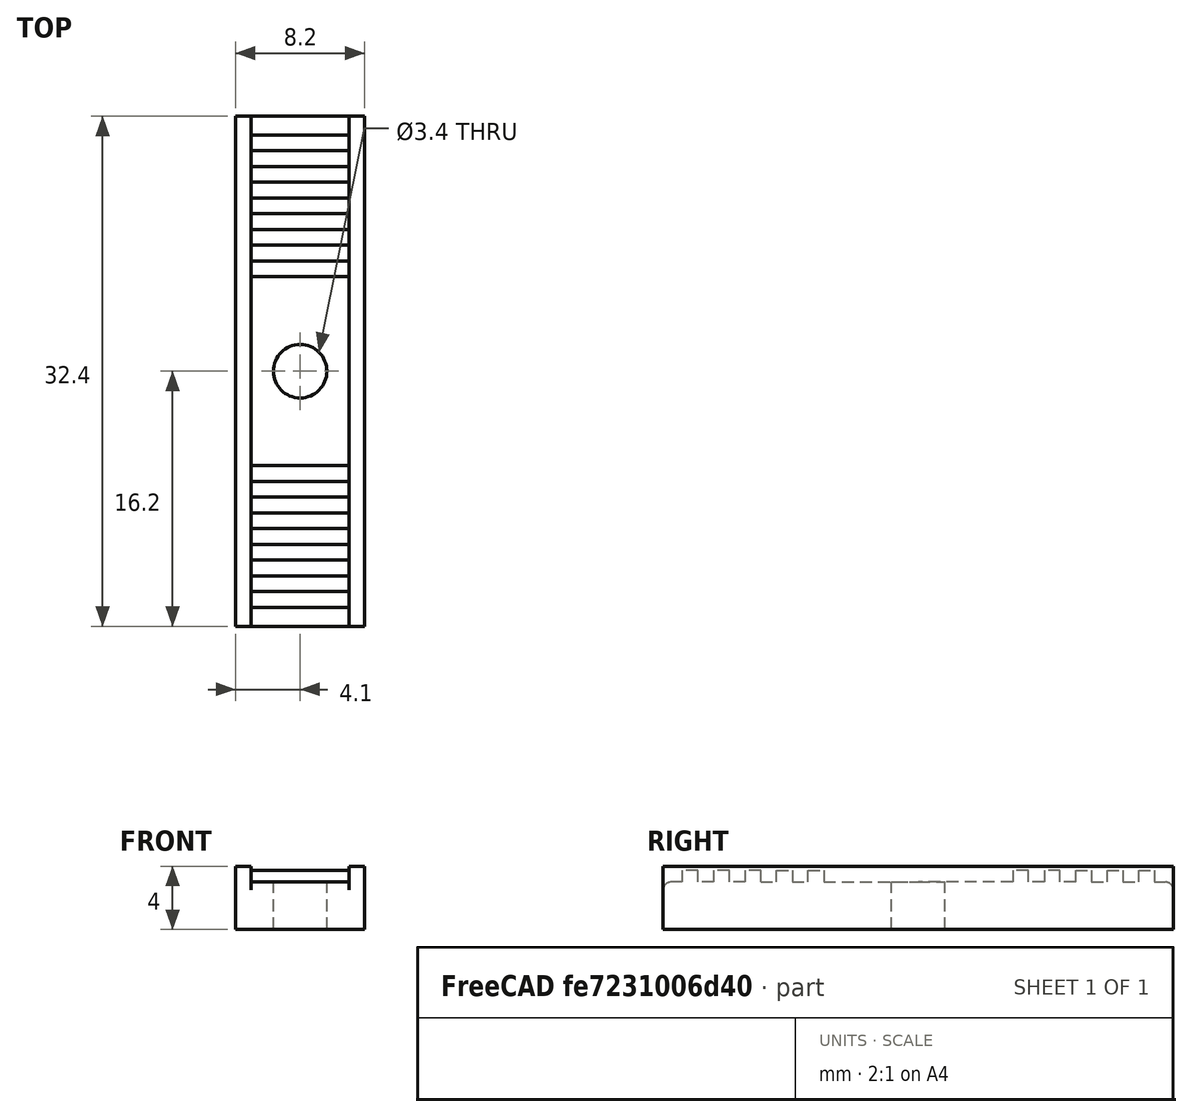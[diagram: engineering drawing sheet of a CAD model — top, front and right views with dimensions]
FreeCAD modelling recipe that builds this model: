
FCSTD DOCUMENT  (FreeCAD 2022.709R28846 (Git))
Label: X_Joiner
License: All rights reserved
LicenseURL: http://en.wikipedia.org/wiki/All_rights_reserved
objects: Sketcher::SketchObject×3, PartDesign::Pad×3, PartDesign::Hole×3, Part::Feature×2, PartDesign::Plane×2, App::DocumentObjectGroup×2, PartDesign::SubShapeBinder×2, PartDesign::Body×2, PartDesign::Fillet×2, Sketcher::SketchExport×2, Spreadsheet::Sheet×1, PartDesign::Mirrored×1, PartDesign::Boolean×1
note: 42 computed .brp shape members not serialized (recipe doc carries the construction recipe); baked Part::Feature solids carry a one-line shape summary decoded from their .brp

FEATURE [Spreadsheet::Sheet] Spreadsheet  label="Variables"
  PythonMode = false
  ShowCells = 0
  TreeRank = 15
  cells = A2=CarriageEdgeToBelt; B2(CarriageEdgeToBelt)==2mm
FEATURE [Part::Feature] XJoint_right_bottom001
  TreeRank = 17
  shape: bbox 38.03 x 54.61 x 16.83 mm, 16460 faces, 0 solids (baked)
FEATURE [PartDesign::Plane] DatumPlane
  AttachmentSupport = -> [XJoint_right_bottom001]
  Length = 49.5
  MapMode = 5
  MinimumLength = 10
  MinimumWidth = 10
  Placement = pos=(0,0,13) rot=(1,0,0;3.14159rad)
  ResizeMode = 0
  Support = -> [XJoint_right_bottom001]
  TreeRank = 13
  Width = 54.5803
FEATURE [Part::Feature] XJoint_right_bottom001_solid  label="XJoint_right_bottom001 (Solid)"
  TreeRank = 26
  shape: bbox 38.03 x 54.61 x 16.83 mm, 16460 faces (baked)
FEATURE [App::DocumentObjectGroup] Group001  label="Base Mesh"
  ClaimAllChildren = true
  ExportMode = 1
  Group = -> [XJoint_right_bottom001]
  TreeRank = 23
  _GroupVersion = 1
FEATURE [PartDesign::SubShapeBinder] Binder  label="Binder(HeatsetLocation)"
  BindCopyOnChange = 0
  BindMode = 0
  ClaimChildren = false
  Context = -> Group [Body.Binder.]
  FillStyle = 0
  Fuse = false
  MakeFace = true
  OffsetFill = false
  OffsetIntersection = false
  OffsetJoinType = 0
  OffsetOpenResult = false
  PartialLoad = false
  Placement = pos=(0,0,6.6) rot=(0,0,1;0rad)
  Relative = true
  Support = -> [Export]
  TreeRank = 27
  _Version = 8
  expr: Placement.Base.z = <<Pad>>.Length
FEATURE [PartDesign::Plane] DatumPlane001
  AttachmentSupport = -> [YZ_Plane001]
  Length = 16.2
  MapMode = 5
  MinimumLength = 10
  MinimumWidth = 10
  Placement = pos=(0,0,0) rot=(0.57735,0.57735,0.57735;2.0944rad)
  ResizeMode = 0
  Support = -> [YZ_Plane001]
  TreeRank = 40
  Width = 10
FEATURE [Sketcher::SketchObject] Sketch001
  ArcFitTolerance = 1e-06
  AttachmentSupport = -> [DatumPlane001]
  FullyConstrained = true
  MapMode = 5
  Placement = pos=(0,0,0) rot=(0.57735,0.57735,0.57735;2.0944rad)
  Support = -> [DatumPlane001]
  TreeRank = 41
  expr: Constraints[50] = <<Sketch>>.Constraints.Length / 2
  expr: Constraints[61] = <<Sketch>>.Constraints[<<Belt Dist>>] / 2
  sketch-geometry (31):
    g0: LineSegment StartX=-10 StartY=3 StartZ=0 EndX=-9 EndY=3 EndZ=0
    g1: LineSegment StartX=-9 StartY=3 StartZ=0 EndX=-9 EndY=3.75 EndZ=0
    g2: LineSegment StartX=-9 StartY=3.75 StartZ=0 EndX=-8 EndY=3.75 EndZ=0
    g3: LineSegment StartX=-8 StartY=3.75 StartZ=0 EndX=-8 EndY=3 EndZ=0
    g4: LineSegment StartX=-7 StartY=3 StartZ=0 EndX=-7 EndY=3.75 EndZ=0
    g5: LineSegment StartX=-10 StartY=3 StartZ=0 EndX=-10 EndY=3.75 EndZ=0
    g6: LineSegment StartX=-10 StartY=3.75 StartZ=0 EndX=-11 EndY=3.75 EndZ=0
    g7: LineSegment StartX=-11 StartY=3.75 StartZ=0 EndX=-11 EndY=3 EndZ=0
    g8: LineSegment StartX=-11 StartY=3 StartZ=0 EndX=-12 EndY=3 EndZ=0
    g9: LineSegment StartX=-12 StartY=3 StartZ=0 EndX=-12 EndY=3.75 EndZ=0
    g10: LineSegment StartX=-12 StartY=3.75 StartZ=0 EndX=-13 EndY=3.75 EndZ=0
    g11: LineSegment StartX=-13 StartY=3.75 StartZ=0 EndX=-13 EndY=3 EndZ=0
    g12: LineSegment [constr] StartX=-12 StartY=3.75 StartZ=0 EndX=-11 EndY=3.75 EndZ=0
    g13: LineSegment [constr] StartX=-10 StartY=3.75 StartZ=0 EndX=-9 EndY=3.75 EndZ=0
    g14: LineSegment [constr] StartX=-8 StartY=3.75 StartZ=0 EndX=-7 EndY=3.75 EndZ=0
    g15: LineSegment [constr] StartX=-10 StartY=3 StartZ=0 EndX=-11 EndY=3 EndZ=0
    g16: LineSegment [constr] StartX=-12 StartY=3 StartZ=0 EndX=-13 EndY=3 EndZ=0
    g17: LineSegment StartX=-16.2 StartY=2.5 StartZ=0 EndX=-16.2 EndY=0 EndZ=0
    g18: LineSegment StartX=-16.2 StartY=0 StartZ=0 EndX=0 EndY=0 EndZ=0
    g19: LineSegment StartX=0 StartY=0 StartZ=0 EndX=0 EndY=3 EndZ=0
    g20: LineSegment StartX=-8 StartY=3 StartZ=0 EndX=-7 EndY=3 EndZ=0
    g21: LineSegment StartX=-7 StartY=3.75 StartZ=0 EndX=-6 EndY=3.75 EndZ=0
    g22: LineSegment StartX=-6 StartY=3.75 StartZ=0 EndX=-6 EndY=3 EndZ=0
    g23: LineSegment StartX=-6 StartY=3 StartZ=0 EndX=0 EndY=3 EndZ=0
    g24: ArcOfCircle CenterX=-15.7 CenterY=2.5 CenterZ=0 NormalX=0 NormalY=0 NormalZ=1 AngleXU=0 Radius=0.5 StartAngle=1.5708 EndAngle=3.14159
    g25: LineSegment StartX=-13 StartY=3 StartZ=0 EndX=-14 EndY=3 EndZ=0
    g26: LineSegment StartX=-14 StartY=3 StartZ=0 EndX=-14 EndY=3.75 EndZ=0
    g27: LineSegment StartX=-14 StartY=3.75 StartZ=0 EndX=-15 EndY=3.75 EndZ=0
    g28: LineSegment StartX=-15 StartY=3.75 StartZ=0 EndX=-15 EndY=3 EndZ=0
    g29: LineSegment StartX=-15 StartY=3 StartZ=0 EndX=-15.7 EndY=3 EndZ=0
    g30: LineSegment [constr] StartX=-14 StartY=3.75 StartZ=0 EndX=-13 EndY=3.75 EndZ=0
  constraints (85):
    c: Horizontal(g0)
    c: Horizontal(g3,g0)
    c: Coincident(g0,g1)
    c: Vertical(g1)
    c: Coincident(g1,g2)
    c: Horizontal(g2)
    c: Coincident(g2,g3)
    c: Vertical(g4)
    c: Coincident(g0,g5)
    c: Vertical(g5)
    c: Coincident(g5,g6)
    c: Horizontal(g6)
    c: Coincident(g6,g7)
    c: Vertical(g7)
    c: Coincident(g7,g8)
    c: Horizontal(g8)
    c: Coincident(g8,g9)
    c: Vertical(g9)
    c: Coincident(g9,g10)
    c: Horizontal(g10)
    c: Coincident(g10,g11)
    c: Vertical(g11)
    c: Coincident(g12,g9)
    c: Coincident(g12,g6)
    c: Horizontal(g12)
    c: Coincident(g13,g5)
    c: Coincident(g13,g1)
    c: Horizontal(g13)
    c: Coincident(g14,g2)
    c: Coincident(g14,g4)
    c: Horizontal(g14)
    c: Coincident(g15,g0)
    c: Coincident(g15,g7)
    c: Coincident(g16,g8)
    c: Coincident(g16,g11)
    c: Horizontal(g15)
    c: Horizontal(g16)
    c: Vertical(g3)
    c: Equal(g10,g6)
    c: Equal(g6,g2)
    c: DistanceX(g10,g6) = 2
    c: DistanceY(g11,g11) = 0.75
    c: Equal(g12,g10)
    c: Equal(g12,g13)
    c: PointOnObject(g17,g-1)
    c: Coincident(g18,g17)
    c: Coincident(g18,g-1)
    c: Coincident(g19,g18)
    c: PointOnObject(g19,g-2)
    c: Vertical(g17)
    c: DistanceX(g17,g18) = 16.2
    c: Coincident(g20,g3)
    c: Coincident(g20,g4)
    c: Horizontal(g20)
    c: Coincident(g21,g4)
    c: Horizontal(g21)
    c: Coincident(g22,g21)
    c: Vertical(g22)
    c: Coincident(g23,g22)
    c: Coincident(g23,g19)
    c: Horizontal(g23)
    c: DistanceX(g23,g23) = 6
    c: Equal(g22,g4)
    c: Equal(g21,g2)
    c: Equal(g14,g13)
    c: DistanceY(g19,g19) = 3
    c: Tangent(g17,g24) = -1.5708
    c: Radius(g24) = 0.5
    c: Coincident(g25,g11)
    c: Horizontal(g25)
    c: Coincident(g26,g25)
    c: Vertical(g26)
    c: Coincident(g27,g26)
    c: Horizontal(g27)
    c: Coincident(g28,g27)
    c: Vertical(g28)
    c: Coincident(g28,g29)
    c: Horizontal(g29)
    c: Horizontal(g28,g25)
    c: Horizontal(g26,g10)
    c: Coincident(g30,g26)
    c: Coincident(g30,g10)
    c: Equal(g30,g12)
    c: Equal(g27,g10)
    c: Tangent(g29,g24) = -1.5708
FEATURE [PartDesign::Pad] Pad001
  ClaimChildren = false
  Direction = (1,1,1)
  Fit = 0
  FitJoin = 0
  InnerFit = 0
  InnerFitJoin = 0
  InnerTaperAngle = 0
  InnerTaperAngleRev = 0
  Length = 6.2
  Length2 = 100
  Linearize = true
  Midplane = true
  NewSolid = false
  Placement = pos=(0,0,0) rot=(0.57735,0.57735,0.57735;2.0944rad)
  Profile = -> Sketch001
  Suppress = false
  TreeRank = 42
  Type = 0
  _ProfileBasedVersion = 1
FEATURE [PartDesign::Mirrored] Mirrored
  BaseFeature = -> Pad001
  CopyShape = false
  MirrorPlane = -> XZ_Plane001
  NewSolid = false
  OriginalSubs = -> [Pad001]
  Originals = -> [Pad001]
  ParallelTransform = true
  Placement = pos=(0,0,0) rot=(0.57735,0.57735,0.57735;2.0944rad)
  SubTransform = true
  Suppress = false
  TreeRank = 43
FEATURE [PartDesign::SubShapeBinder] Reference  label="Reference(XJoint_right_bottom001 (Solid))"
  BindCopyOnChange = 0
  BindMode = 0
  ClaimChildren = false
  Context = -> Group [Body.Reference.]
  FillStyle = 0
  Fuse = false
  MakeFace = true
  OffsetFill = false
  OffsetIntersection = false
  OffsetJoinType = 0
  OffsetOpenResult = false
  PartialLoad = false
  Relative = true
  Support = -> [XJoint_right_bottom001_solid]
  TreeRank = 49
  _Version = 8
FEATURE [App::DocumentObjectGroup] Group  label="Right"
  ClaimAllChildren = true
  ExportMode = 1
  Group = -> [Group001,XJoint_right_bottom001_solid,Body,Body001]
  TreeRank = 16
  _GroupVersion = 1
FEATURE [PartDesign::Body] Body  label="XJoint_Right"
  AutoGroupSolids = false
  ClaimAllChildren = false
  ExportMode = 0
  Group = -> [DatumPlane,Sketch,Pad,Fillet,Fillet001,Export,Binder,Hole,Hole001,Boolean]
  Origin = -> Origin
  Tip = -> Boolean
  TreeRank = 25
  _ExportChildren = -> [DatumPlane,Pad,Fillet,Fillet001,Hole,Hole001,Boolean]
  _GroupVersion = 1
FEATURE [Sketcher::SketchObject] Sketch
  ArcFitTolerance = 1e-06
  AttachmentSupport = -> [DatumPlane]
  Exports = -> [Export]
  FullyConstrained = true
  MapMode = 5
  Placement = pos=(0,0,13) rot=(1,0,0;3.14159rad)
  Support = -> [DatumPlane]
  TreeRank = 14
  expr: Constraints[47] = <<Variables>>.CarriageEdgeToBelt
  sketch-geometry (28):
    g0: Circle [constr] CenterX=-10 CenterY=10 CenterZ=0 NormalX=0 NormalY=0 NormalZ=1 AngleXU=0 Radius=1.5
    g1: Circle [constr] CenterX=10 CenterY=10 CenterZ=0 NormalX=0 NormalY=0 NormalZ=1 AngleXU=0 Radius=1.5
    g2: Circle [constr] CenterX=10 CenterY=-10 CenterZ=0 NormalX=0 NormalY=0 NormalZ=1 AngleXU=0 Radius=1.5
    g3: Circle [constr] CenterX=-10 CenterY=-10 CenterZ=0 NormalX=0 NormalY=0 NormalZ=1 AngleXU=0 Radius=1.5
    g4: Circle [constr] CenterX=18.75 CenterY=0 CenterZ=0 NormalX=0 NormalY=0 NormalZ=1 AngleXU=0 Radius=3
    g5: LineSegment StartX=15.5 StartY=8 StartZ=0 EndX=22 EndY=8 EndZ=0
    g6: LineSegment StartX=22 StartY=8 StartZ=0 EndX=22 EndY=6 EndZ=0
    g7: LineSegment StartX=22 StartY=6 StartZ=0 EndX=15.5 EndY=6 EndZ=0
    g8: LineSegment StartX=15.5 StartY=6 StartZ=0 EndX=15.5 EndY=8 EndZ=0
    g9: LineSegment StartX=15.5 StartY=-6 StartZ=0 EndX=22 EndY=-6 EndZ=0
    g10: LineSegment StartX=22 StartY=-6 StartZ=0 EndX=22 EndY=-8 EndZ=0
    g11: LineSegment StartX=22 StartY=-8 StartZ=0 EndX=15.5 EndY=-8 EndZ=0
    g12: LineSegment StartX=15.5 StartY=-8 StartZ=0 EndX=15.5 EndY=-6 EndZ=0
    g13: LineSegment StartX=6 StartY=-16.2 StartZ=0 EndX=23 EndY=-16.2 EndZ=0
    g14: LineSegment StartX=25 StartY=-14.2 StartZ=0 EndX=25 EndY=14.2 EndZ=0
    g15: LineSegment StartX=23 StartY=16.2 StartZ=0 EndX=6 EndY=16.2 EndZ=0
    g16: LineSegment StartX=6 StartY=16.2 StartZ=0 EndX=6 EndY=-16.2 EndZ=0
    g17: LineSegment [constr] StartX=-13.5 StartY=16.2 StartZ=0 EndX=13.5 EndY=16.2 EndZ=0
    g18: LineSegment [constr] StartX=13.5 StartY=16.2 StartZ=0 EndX=13.5 EndY=-16.2 EndZ=0
    g19: LineSegment [constr] StartX=13.5 StartY=-16.2 StartZ=0 EndX=-13.5 EndY=-16.2 EndZ=0
    g20: LineSegment [constr] StartX=-13.5 StartY=-16.2 StartZ=0 EndX=-13.5 EndY=16.2 EndZ=0
    g21: ArcOfCircle CenterX=23 CenterY=14.2 CenterZ=0 NormalX=0 NormalY=0 NormalZ=1 AngleXU=0 Radius=2 StartAngle=3e-16 EndAngle=1.5708
    g22: GeomPoint [constr] X=25 Y=16.2 Z=0
    g23: ArcOfCircle CenterX=23 CenterY=-14.2 CenterZ=0 NormalX=0 NormalY=0 NormalZ=1 AngleXU=0 Radius=2 StartAngle=4.71239 EndAngle=6.28319
    g24: GeomPoint [constr] X=25 Y=-16.2 Z=0
    g25: Circle CenterX=10 CenterY=10 CenterZ=0 NormalX=0 NormalY=0 NormalZ=1 AngleXU=0 Radius=3
    g26: Circle CenterX=10 CenterY=-10 CenterZ=0 NormalX=0 NormalY=0 NormalZ=1 AngleXU=0 Radius=3
    g27: LineSegment [constr] StartX=18.75 StartY=6 StartZ=0 EndX=18.75 EndY=-6 EndZ=0
  constraints (73):
    c: Symmetric(g3,g2,g-2)
    c: Symmetric(g0,g1,g-2)
    c: Symmetric(g3,g0,g-1)
    c: DistanceX(g0,g1) = 20
    c: DistanceY(g3,g0) = 20
    c: Radius(g0) = 1.5
    c: Equal(g0,g1)
    c: Equal(g0,g2)
    c: Equal(g0,g3)
    c: PointOnObject(g4,g-1)
    c: Coincident(g5,g6)
    c: Coincident(g6,g7)
    c: Coincident(g7,g8)
    c: Coincident(g8,g5)
    c: Horizontal(g5)
    c: Horizontal(g7)
    c: Vertical(g6)
    c: Vertical(g8)
    c: Coincident(g9,g10)
    c: Coincident(g10,g11)
    c: Coincident(g11,g12)
    c: Coincident(g12,g9)
    c: Horizontal(g9)
    c: Horizontal(g11)
    c: Vertical(g10)
    c: Vertical(g12)
    c: Equal(g9,g7)
    c: Equal(g10,g6)
    c: Symmetric(g6,g9,g-1)
    c: DistanceX(g11,g11) = 6.5
    c: DistanceY(g12,g12) = 2
    c: Diameter(g4) = 6
    c: Horizontal(g13)
    c: Vertical(g14)
    c: Horizontal(g15)
    c: Coincident(g15,g16)
    c: Coincident(g13,g16)
    c: Coincident(g17,g18)
    c: Coincident(g18,g19)
    c: Coincident(g19,g20)
    c: Coincident(g20,g17)
    c: Horizontal(g17)
    c: Vertical(g18)
    c: Symmetric(g18,g19,g-2)
    c: DistanceX(g17,g17) = 27
    c: DistanceY(g20,g20) = 32.4
    c: Symmetric(g19,g17,g-1)
    c: DistanceX(g17,g5) = 2
    c: DistanceX(g5,g22) = 3
    c: PointOnObject(g22,g15)
    c: PointOnObject(g22,g14)
    c: Tangent(g15,g21) = -1.5708
    c: Tangent(g14,g21) = -1.5708
    c: PointOnObject(g24,g14)
    c: PointOnObject(g24,g13)
    c: Tangent(g14,g23) = -1.5708
    c: Tangent(g13,g23) = -1.5708
    c: Coincident(g25,g1)
    c: Coincident(g26,g2)
    c: PointOnObject(g27,g7)
    c: Vertical(g27)
    c: Symmetric(g9,g9,g27)
    c: PointOnObject(g4,g27)
    c: DistanceY(g4,g27) = 6
    c: Equal(g16,g18)
    c: Symmetric(g15,g13,g-1)
    c: Radius(g21) = 2
    c: Equal(g23,g21)
    c: Diameter(g26) = 6
    c: Equal(g26,g25)
    c: DistanceX(g13,g26) = 4
    c: DistanceY(g24,g22) = 32.4  'Length'
    c: DistanceY(g27,g27) = 12  'Belt Dist'
FEATURE [PartDesign::Pad] Pad
  ClaimChildren = false
  Direction = (1,1,1)
  Fit = 0
  FitJoin = 0
  InnerFit = 0
  InnerFitJoin = 0
  InnerTaperAngle = 0
  InnerTaperAngleRev = 0
  Length = 6.6
  Length2 = 100
  Linearize = true
  NewSolid = false
  Placement = pos=(0,0,13) rot=(1,0,0;3.14159rad)
  Profile = -> Sketch
  Reversed = true
  Suppress = false
  TreeRank = 18
  Type = 0
  _ProfileBasedVersion = 1
FEATURE [PartDesign::Fillet] Fillet
  Base = -> Pad [Edge24,Edge21]
  BaseFeature = -> Pad
  NewSolid = false
  Placement = pos=(0,0,13) rot=(1,0,0;3.14159rad)
  Radius = 0.6
  SupportTransform = false
  Suppress = false
  TreeRank = 19
FEATURE [PartDesign::Fillet] Fillet001
  Base = -> Fillet [Edge22]
  BaseFeature = -> Fillet
  NewSolid = false
  Placement = pos=(0,0,13) rot=(1,0,0;3.14159rad)
  Radius = 2
  SupportTransform = false
  Suppress = false
  TreeRank = 20
FEATURE [Sketcher::SketchExport] Export  label="HeatsetLocation"
  Base = -> Sketch
  BaseRefs = -> Sketch [edge5]
  Placement = pos=(0,0,13) rot=(1,0,0;3.14159rad)
  Refs = ;g5.edge5
  SyncPlacement = true
  TreeRank = 24
FEATURE [PartDesign::Hole] Hole
  BaseFeature = -> Fillet001
  ClaimChildren = false
  CustomThreadClearance = 0
  Depth = 25
  DepthType = 0
  Diameter = 3.4
  DrillForDepth = false
  DrillPoint = 1
  DrillPointAngle = 118
  Fit = 0
  FitJoin = 0
  HoleCutCountersinkAngle = 90
  HoleCutCustomValues = false
  HoleCutDepth = 0
  HoleCutDiameter = 6.1
  HoleCutType = 0
  InnerFit = 0
  InnerFitJoin = 0
  ModelThread = false
  NewSolid = false
  Placement = pos=(0,0,13) rot=(1,0,0;3.14159rad)
  Profile = -> Binder
  Suppress = false
  Tapered = false
  TaperedAngle = 90
  ThreadClass = 0
  ThreadDepth = 25
  ThreadDepthType = 0
  ThreadDirection = 0
  ThreadFit = 0
  ThreadSize = 9
  ThreadType = 1
  Threaded = false
  TreeRank = 28
  UseCustomThreadClearance = false
  _ProfileBasedVersion = 1
FEATURE [PartDesign::Hole] Hole001
  BaseFeature = -> Hole
  ClaimChildren = false
  CustomThreadClearance = 0
  Depth = 5
  DepthType = 0
  Diameter = 5
  DrillForDepth = false
  DrillPoint = 0
  DrillPointAngle = 118
  Fit = 0
  FitJoin = 0
  HoleCutCountersinkAngle = 90
  HoleCutCustomValues = false
  HoleCutDepth = 0
  HoleCutDiameter = 6.1
  HoleCutType = 0
  InnerFit = 0
  InnerFitJoin = 0
  ModelThread = false
  NewSolid = false
  Placement = pos=(0,0,13) rot=(1,0,0;3.14159rad)
  Profile = -> Binder
  Suppress = false
  Tapered = true
  TaperedAngle = 88
  ThreadClass = 0
  ThreadDepth = 5
  ThreadDepthType = 0
  ThreadDirection = 0
  ThreadFit = 0
  ThreadSize = 0
  ThreadType = 0
  Threaded = false
  TreeRank = 29
  UseCustomThreadClearance = false
  _ProfileBasedVersion = 1
FEATURE [PartDesign::Body] Body001  label="BeltClamp"
  AutoGroupSolids = false
  ClaimAllChildren = false
  ExportMode = 0
  Group = -> [DatumPlane001,Sketch001,Pad001,Mirrored,Sketch002,Pad002,Export001,Hole002]
  Origin = -> Origin001
  Placement = pos=(18.8,0,8.8) rot=(0,0,1;0rad)
  Tip = -> Hole002
  TreeRank = 39
  _ExportChildren = -> [DatumPlane001,Pad001,Mirrored,Pad002,Hole002]
  _GroupVersion = 1
FEATURE [Sketcher::SketchObject] Sketch002
  ArcFitTolerance = 1e-06
  AttachmentSupport = -> [XY_Plane001]
  Exports = -> [Export001]
  FullyConstrained = true
  MapMode = 5
  Support = -> [XY_Plane001]
  TreeRank = 44
  expr: Constraints[20] = <<Pad001>>.Length
  expr: Constraints[22] = <<Sketch>>.Constraints.Length
  sketch-geometry (9):
    g0: Circle [constr] CenterX=0 CenterY=0 CenterZ=0 NormalX=0 NormalY=0 NormalZ=1 AngleXU=0 Radius=1.5
    g1: LineSegment StartX=-4.1 StartY=16.2 StartZ=0 EndX=-3.1 EndY=16.2 EndZ=0
    g2: LineSegment StartX=-3.1 StartY=16.2 StartZ=0 EndX=-3.1 EndY=-16.2 EndZ=0
    g3: LineSegment StartX=-3.1 StartY=-16.2 StartZ=0 EndX=-4.1 EndY=-16.2 EndZ=0
    g4: LineSegment StartX=-4.1 StartY=-16.2 StartZ=0 EndX=-4.1 EndY=16.2 EndZ=0
    g5: LineSegment StartX=4.1 StartY=-16.2 StartZ=0 EndX=3.1 EndY=-16.2 EndZ=0
    g6: LineSegment StartX=3.1 StartY=-16.2 StartZ=0 EndX=3.1 EndY=16.2 EndZ=0
    g7: LineSegment StartX=3.1 StartY=16.2 StartZ=0 EndX=4.1 EndY=16.2 EndZ=0
    g8: LineSegment StartX=4.1 StartY=16.2 StartZ=0 EndX=4.1 EndY=-16.2 EndZ=0
  constraints (24):
    c: Coincident(g0,g-1)
    c: Diameter(g0) = 3
    c: Coincident(g1,g2)
    c: Coincident(g2,g3)
    c: Coincident(g3,g4)
    c: Coincident(g4,g1)
    c: Horizontal(g1)
    c: Horizontal(g3)
    c: Vertical(g2)
    c: Vertical(g4)
    c: Coincident(g5,g6)
    c: Coincident(g6,g7)
    c: Coincident(g7,g8)
    c: Coincident(g8,g5)
    c: Horizontal(g5)
    c: Horizontal(g7)
    c: Vertical(g6)
    c: Equal(g7,g1)
    c: DistanceX(g1,g1) = 1
    c: Symmetric(g6,g1,g-2)
    c: DistanceX(g1,g6) = 6.2
    c: Symmetric(g5,g7,g-1)
    c: DistanceY(g8,g8) = 32.4
    c: Equal(g2,g6)
FEATURE [PartDesign::Pad] Pad002
  BaseFeature = -> Mirrored
  ClaimChildren = false
  Direction = (1,1,1)
  Fit = 0
  FitJoin = 0
  InnerFit = 0
  InnerFitJoin = 0
  InnerTaperAngle = 0
  InnerTaperAngleRev = 0
  Length = 4
  Length2 = 100
  Linearize = true
  NewSolid = false
  Placement = pos=(0,0,0) rot=(0.57735,0.57735,0.57735;2.0944rad)
  Profile = -> Sketch002
  Suppress = false
  TreeRank = 45
  Type = 0
  _ProfileBasedVersion = 1
FEATURE [Sketcher::SketchExport] Export001
  Base = -> Sketch002
  BaseRefs = -> Sketch002 [edge1]
  Refs = ;g1.edge1
  SyncPlacement = true
  TreeRank = 46
FEATURE [PartDesign::Hole] Hole002
  BaseFeature = -> Pad002
  ClaimChildren = false
  CustomThreadClearance = 0
  Depth = 25
  DepthType = 0
  Diameter = 3.4
  DrillForDepth = false
  DrillPoint = 1
  DrillPointAngle = 118
  Fit = 0
  FitJoin = 0
  HoleCutCountersinkAngle = 90
  HoleCutCustomValues = false
  HoleCutDepth = 0
  HoleCutDiameter = 6.1
  HoleCutType = 0
  InnerFit = 0
  InnerFitJoin = 0
  ModelThread = false
  NewSolid = false
  Placement = pos=(0,0,0) rot=(0.57735,0.57735,0.57735;2.0944rad)
  Profile = -> Export001
  Reversed = true
  Suppress = false
  Tapered = false
  TaperedAngle = 90
  ThreadClass = 0
  ThreadDepth = 25
  ThreadDepthType = 0
  ThreadDirection = 0
  ThreadFit = 0
  ThreadSize = 9
  ThreadType = 1
  Threaded = false
  TreeRank = 47
  UseCustomThreadClearance = false
  _ProfileBasedVersion = 1
FEATURE [PartDesign::Boolean] Boolean
  BaseFeature = -> Hole001
  ClaimAllChildren = false
  ExportMode = 0
  Group = -> [Reference]
  NewSolid = false
  Suppress = false
  TreeRank = 48
  Type = 0
  _ExportChildren = -> [Reference]
  _GroupVersion = 1
